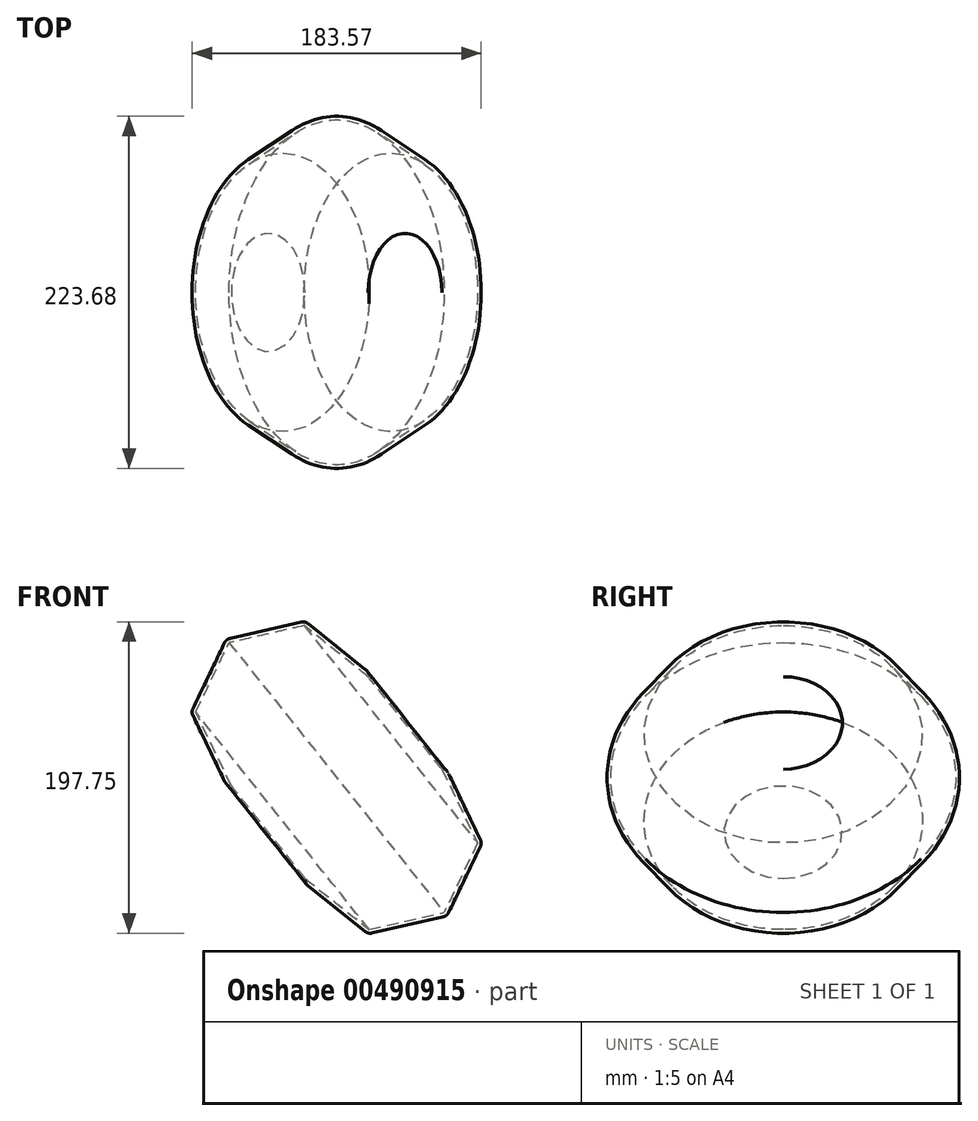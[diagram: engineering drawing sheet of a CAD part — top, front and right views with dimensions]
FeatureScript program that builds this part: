
annotation { "Feature Type Name" : "Feature", "Feature Type Description" : "" }
export const myFeature = defineFeature(function(context is Context, id is Id, definition is map)
    precondition{}
    {
        {
            var Q0;
            Q0=qCreatedBy(makeId("Front.planeOp"),FACE);
            var sketch = newSketch(context, id + "F0", { "sketchPlane" : qUnion([Q0])});
            skCircle(sketch, "E0.cCircle", {"center": v(0, 0) * mm, "radius": 59.13 * mm, "construction": true});
            skLineSegment(sketch, "E0.0", {"start": v(59.13, 0) * mm, "end": v(36.86, -46.23) * mm});
            skLineSegment(sketch, "E0.1", {"start": v(36.86, -46.23) * mm, "end": v(-13.16, -57.64) * mm});
            skLineSegment(sketch, "E0.2", {"start": v(-13.16, -57.64) * mm, "end": v(-53.27, -25.65) * mm});
            skLineSegment(sketch, "E0.3", {"start": v(-53.27, -25.65) * mm, "end": v(-53.27, 25.65) * mm});
            skLineSegment(sketch, "E0.4", {"start": v(-53.27, 25.65) * mm, "end": v(-13.16, 57.64) * mm});
            skLineSegment(sketch, "E0.5", {"start": v(-13.16, 57.64) * mm, "end": v(36.86, 46.23) * mm});
            skLineSegment(sketch, "E0.6", {"start": v(36.86, 46.23) * mm, "end": v(59.13, 0) * mm});
            skSolve(sketch);
        }
        {
            var Q0;
            Q0=makeQuery(id+"F0.imprint","IMPRINT",FACE,{"disambiguationData":[TD([[makeQuery(id+"F0.imprint","IMPRINT",EDGE,{"derivedFrom":sQuery(id+"F0.wireOp",EDGE,"E0.0")}),-1.0]])]});
            var Q1;
            Q1=sQuery(id+"F0.wireOp",EDGE,"E0.4");
            revolve(context, id + "F1", {"entities" : qUnion([Q0]), "axis" : qUnion([Q1]), "revolveType" : RevolveType.FULL});
        }
        {
            var Q0;
            Q0=makeQuery(id+"F1.opRevolve","SWEPT_FACE",FACE,{"disambiguationData":[OSD([sQuery(id+"F0.wireOp",EDGE,"E0.3")])]});
            var Q1;
            Q1=makeQuery(id+"F1.opRevolve","SWEPT_FACE",FACE,{"disambiguationData":[OSD([sQuery(id+"F0.wireOp",EDGE,"E0.5")])]});
            shell(context, id + "F2", {"entities" : qUnion([Q0, Q1]), "thickness" : 2.54 * mm});
        }
        {
            var Q0;
            Q0=makeQuery(id+"F1.opRevolve","SWEPT_EDGE",EDGE,{"disambiguationData":[OSD([sQuery(id+"F0.wireOp",EDGE,"E0.0"),sQuery(id+"F0.wireOp",EDGE,"E0.1")])]});
            fillet(context, id + "F3", {"entities" : qUnion([Q0]), "radius" : 5.08 * mm, "tangentPropagation" : true, "allowEdgeOverflow" : false});
        }
        {
            var Q0;
            Q0=makeQuery(id+"F1.opRevolve","SWEPT_EDGE",EDGE,{"disambiguationData":[OSD([sQuery(id+"F0.wireOp",EDGE,"E0.0"),sQuery(id+"F0.wireOp",EDGE,"E0.6")])]});
            var Q1;
            Q1=makeQuery(id+"F1.opRevolve","SWEPT_EDGE",EDGE,{"disambiguationData":[OSD([sQuery(id+"F0.wireOp",EDGE,"E0.1"),sQuery(id+"F0.wireOp",EDGE,"E0.2")])]});
            fillet(context, id + "F4", {"entities" : qUnion([Q0, Q1]), "radius" : 5.08 * mm, "tangentPropagation" : true, "allowEdgeOverflow" : false});
        }
        {
            var Q0;
            Q0=makeQuery(id+"F1.opRevolve","SWEPT_EDGE",EDGE,{"disambiguationData":[OSD([sQuery(id+"F0.wireOp",EDGE,"E0.5"),sQuery(id+"F0.wireOp",EDGE,"E0.6")])]});
            var Q1;
            Q1=makeQuery(id+"F1.opRevolve","SWEPT_EDGE",EDGE,{"disambiguationData":[OSD([sQuery(id+"F0.wireOp",EDGE,"E0.2"),sQuery(id+"F0.wireOp",EDGE,"E0.3")])]});
            var Q2;
            {var subQ0=sQuery(id+"F0.wireOp",EDGE,"E0.0");Q2=makeQuery(id+"F3.opFillet","BLEND_EDGE",EDGE,{"blendedFrom":[makeQuery(id+"F1.opRevolve","SWEPT_EDGE",EDGE,{"disambiguationData":[OSD([subQ0,sQuery(id+"F0.wireOp",EDGE,"E0.1")])]}),makeQuery(id+"F1.opRevolve","SWEPT_FACE",FACE,{"disambiguationData":[OSD([subQ0])]})],"blendedInto":[makeQuery(id+"F1.opRevolve","SWEPT_FACE",FACE,{"disambiguationData":[OSD([subQ0])]})]});}
            var Q3;
            {var subQ0=sQuery(id+"F0.wireOp",EDGE,"E0.1");Q3=makeQuery(id+"F3.opFillet","BLEND_EDGE",EDGE,{"blendedFrom":[makeQuery(id+"F1.opRevolve","SWEPT_EDGE",EDGE,{"disambiguationData":[OSD([sQuery(id+"F0.wireOp",EDGE,"E0.0"),subQ0])]}),makeQuery(id+"F1.opRevolve","SWEPT_FACE",FACE,{"disambiguationData":[OSD([subQ0])]})],"blendedInto":[makeQuery(id+"F1.opRevolve","SWEPT_FACE",FACE,{"disambiguationData":[OSD([subQ0])]})]});}
            fillet(context, id + "F5", {"entities" : qUnion([Q0, Q1, Q2, Q3]), "radius" : 5.08 * mm, "tangentPropagation" : true, "allowEdgeOverflow" : false});
        }
    });
